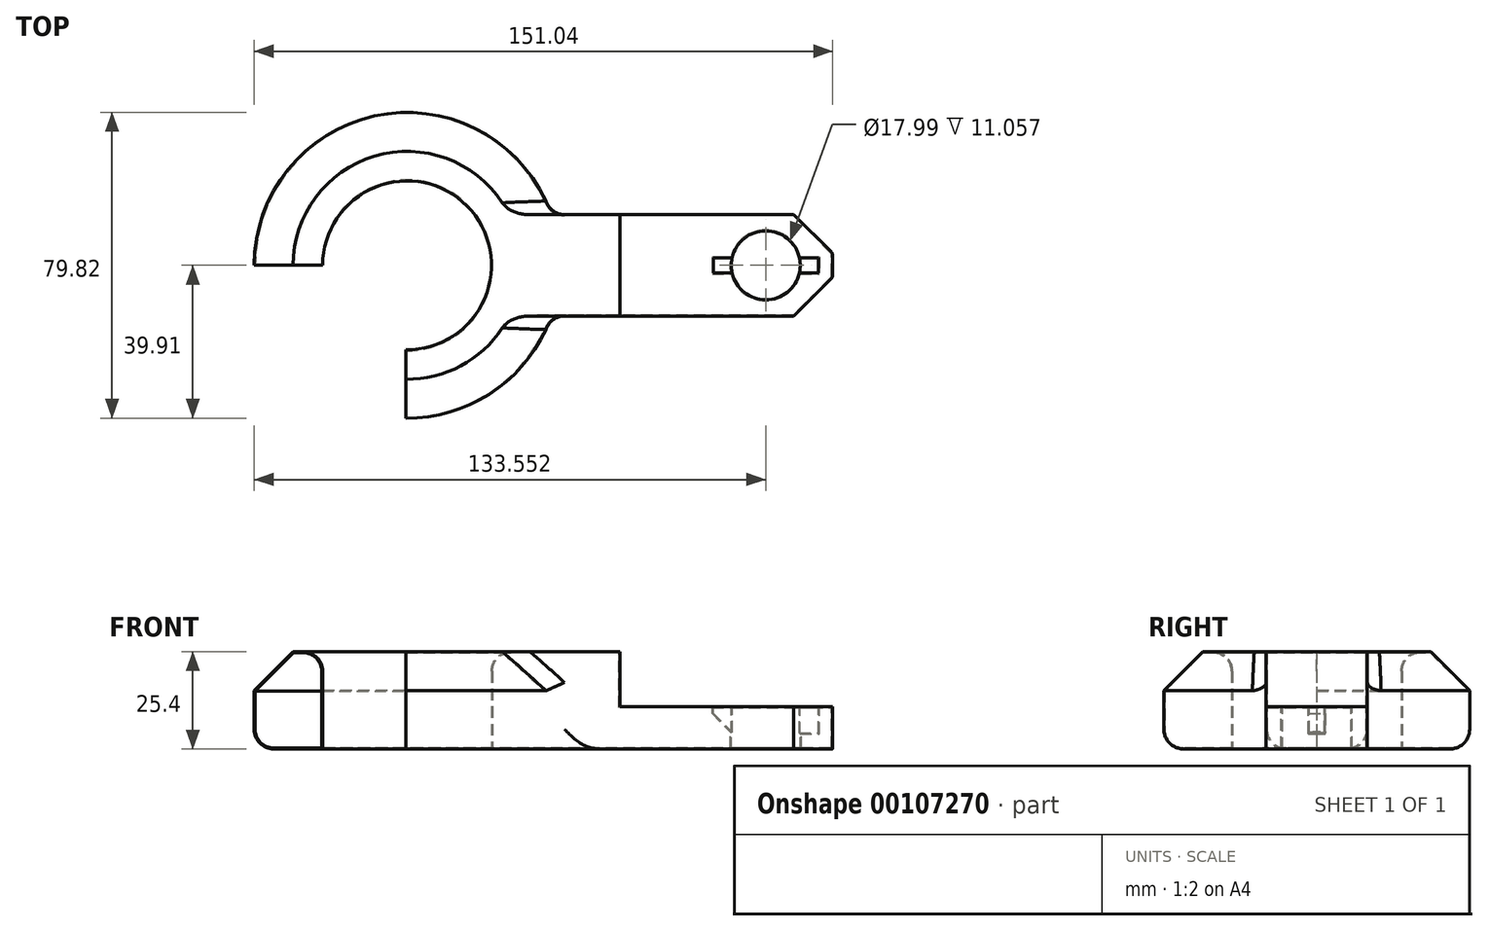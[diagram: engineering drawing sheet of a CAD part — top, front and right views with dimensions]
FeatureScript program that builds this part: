
annotation { "Feature Type Name" : "Feature", "Feature Type Description" : "" }
export const myFeature = defineFeature(function(context is Context, id is Id, definition is map)
    precondition{}
    {
        {
            var Q0;
            Q0=qCreatedBy(makeId("Top.planeOp"),FACE);
            var sketch = newSketch(context, id + "F0", { "sketchPlane" : qUnion([Q0])});
            skLineSegment(sketch, "E0.bottom", {"start": v(55.56, -13.22) * mm, "end": v(-55.56, -13.22) * mm});
            skLineSegment(sketch, "E0.top", {"start": v(55.56, 13.22) * mm, "end": v(-55.56, 13.22) * mm});
            skLineSegment(sketch, "E0.left", {"start": v(55.56, -13.22) * mm, "end": v(55.56, 13.22) * mm});
            skLineSegment(sketch, "E0.right", {"start": v(-55.56, -13.22) * mm, "end": v(-55.56, 13.22) * mm});
            skPoint(sketch, "E0.middle", {"position": v(0, 0) * mm});
            skCircle(sketch, "E1", {"center": v(-55.56, 0) * mm, "radius": 39.91 * mm});
            skCircle(sketch, "E2", {"center": v(-55.56, 0) * mm, "radius": 22.04 * mm});
            skSolve(sketch);
        }
        {
            var Q0;
            {var subQ0=sQuery(id+"F0.wireOp",EDGE,"E1");var subQ1=sQuery(id+"F0.wireOp",EDGE,"E0.bottom");var subQ2=makeQuery(id+"F0.imprint","INTERSECT",VERTEX,{"derivedFrom":[subQ1,subQ0]});Q0=makeQuery(id+"F0.imprint","IMPRINT",FACE,{"disambiguationData":[TD([[makeQuery(id+"F0.imprint","IMPRINT",EDGE,{"disambiguationData":[TD([[subQ2,-1.0]])],"derivedFrom":subQ1}),1.0]])]});}
            var Q1;
            {var subQ0=sQuery(id+"F0.wireOp",EDGE,"E1");var subQ1=sQuery(id+"F0.wireOp",EDGE,"E0.bottom");var subQ2=makeQuery(id+"F0.imprint","INTERSECT",VERTEX,{"derivedFrom":[subQ1,subQ0]});Q1=makeQuery(id+"F0.imprint","IMPRINT",FACE,{"disambiguationData":[TD([[makeQuery(id+"F0.imprint","IMPRINT",EDGE,{"disambiguationData":[TD([[subQ2,-1.0]])],"derivedFrom":subQ1}),-1.0]])]});}
            var Q2;
            {var subQ0=sQuery(id+"F0.wireOp",EDGE,"E0.left");Q2=makeQuery(id+"F0.imprint","IMPRINT",FACE,{"disambiguationData":[TD([[makeQuery(id+"F0.imprint","IMPRINT",EDGE,{"derivedFrom":subQ0}),1.0]])]});}
            extrude(context, id + "F1", {"entities" : qUnion([Q0, Q1, Q2]), "depth" : 25.4 * mm});
        }
        {
            var Q0;
            Q0=makeQuery(id+"F1.opExtrude","CAP_FACE",FACE,{"disambiguationData":[OSD([sQuery(id+"F0.wireOp",EDGE,"E0.bottom"),sQuery(id+"F0.wireOp",EDGE,"E0.top"),sQuery(id+"F0.wireOp",EDGE,"E0.left"),sQuery(id+"F0.wireOp",EDGE,"E1"),sQuery(id+"F0.wireOp",EDGE,"E2")])],"isStart":false});
            var sketch = newSketch(context, id + "F2", { "sketchPlane" : qUnion([Q0])});
            skLineSegment(sketch, "E3.bottom", {"start": v(12.25, 19.58) * mm, "end": v(60.23, 19.58) * mm});
            skLineSegment(sketch, "E3.top", {"start": v(12.25, -22.04) * mm, "end": v(60.23, -22.04) * mm});
            skLineSegment(sketch, "E3.left", {"start": v(12.25, 19.58) * mm, "end": v(12.25, -22.04) * mm});
            skLineSegment(sketch, "E3.right", {"start": v(60.23, 19.58) * mm, "end": v(60.23, -22.04) * mm});
            skSolve(sketch);
        }
        {
            var Q0;
            {var subQ5=makeQuery(id+"F1.opExtrude","CAP_EDGE",EDGE,{"disambiguationData":[OSD([sQuery(id+"F0.wireOp",EDGE,"E0.left")])],"isStart":false});Q0=makeQuery(id+"F2.imprint","IMPRINT",FACE,{"disambiguationData":[TD([[makeQuery(id+"F2.imprint","IMPRINT",EDGE,{"derivedFrom":subQ5}),1.0]])]});}
            extrude(context, id + "F3", {"entities" : qUnion([Q0]), "operationType" : NewBodyOperationType.ADD, "oppositeDirection" : true, "depth" : 15.04 * mm});
        }
        {
            var Q0;
            Q0=makeQuery(id+"F1.opExtrude","CAP_FACE",FACE,{"disambiguationData":[OSD([sQuery(id+"F0.wireOp",EDGE,"E0.bottom"),sQuery(id+"F0.wireOp",EDGE,"E0.top"),sQuery(id+"F0.wireOp",EDGE,"E0.left"),sQuery(id+"F0.wireOp",EDGE,"E1"),sQuery(id+"F0.wireOp",EDGE,"E2")])],"isStart":false});
            var sketch = newSketch(context, id + "F4", { "sketchPlane" : qUnion([Q0])});
            skLineSegment(sketch, "E4.bottom", {"start": v(0, 13.22) * mm, "end": v(55.56, 13.22) * mm});
            skLineSegment(sketch, "E4.top", {"start": v(0, -13.22) * mm, "end": v(55.56, -13.22) * mm});
            skLineSegment(sketch, "E4.left", {"start": v(0, 13.22) * mm, "end": v(0, -13.22) * mm});
            skLineSegment(sketch, "E4.right", {"start": v(55.56, 13.22) * mm, "end": v(55.56, -13.22) * mm});
            skSolve(sketch);
        }
        {
            var Q0;
            Q0=makeQuery(id+"F4.imprint","IMPRINT",FACE,{"disambiguationData":[TD([[makeQuery(id+"F4.imprint","IMPRINT",EDGE,{"derivedFrom":sQuery(id+"F4.wireOp",EDGE,"E4.bottom")}),1.0]])]});
            extrude(context, id + "F5", {"entities" : qUnion([Q0]), "operationType" : NewBodyOperationType.REMOVE, "oppositeDirection" : true, "depth" : 14.34 * mm});
        }
        {
            var Q0;
            Q0=makeQuery(id+"F5.boolean.opBoolean","COPY",EDGE,{"derivedFrom":makeQuery(id+"F5.opExtrude","CAP_EDGE",EDGE,{"disambiguationData":[OSD([sQuery(id+"F4.wireOp",EDGE,"E4.left")])],"isStart":true})});
            var Q1;
            Q1=makeQuery(id+"F1.opExtrude","CAP_EDGE",EDGE,{"disambiguationData":[OSD([sQuery(id+"F0.wireOp",EDGE,"E1")])],"isStart":false});
            var Q2;
            Q2=makeQuery(id+"F1.opExtrude","SWEPT_EDGE",EDGE,{"disambiguationData":[OSD([sQuery(id+"F0.wireOp",EDGE,"E0.bottom"),sQuery(id+"F0.wireOp",EDGE,"E0.left")])]});
            var Q3;
            Q3=makeQuery(id+"F1.opExtrude","SWEPT_EDGE",EDGE,{"disambiguationData":[OSD([sQuery(id+"F0.wireOp",EDGE,"E0.top"),sQuery(id+"F0.wireOp",EDGE,"E0.left")])]});
            chamfer(context, id + "F6", {"entities" : qUnion([Q0, Q1, Q2, Q3]), "width" : 10.16 * mm, "tangentPropagation" : true});
        }
        {
            var Q0;
            Q0=makeQuery(id+"F6.opChamfer","BLEND_EDGE",EDGE,{"blendedFrom":[makeQuery(id+"F1.opExtrude","CAP_EDGE",EDGE,{"disambiguationData":[OSD([sQuery(id+"F0.wireOp",EDGE,"E1")])],"isStart":false}),makeQuery(id+"F1.opExtrude","SWEPT_FACE",FACE,{"disambiguationData":[OSD([sQuery(id+"F0.wireOp",EDGE,"E0.top")])]})],"blendedInto":[makeQuery(id+"F1.opExtrude","SWEPT_FACE",FACE,{"disambiguationData":[OSD([sQuery(id+"F0.wireOp",EDGE,"E0.top")])]})]});
            var Q1;
            Q1=makeQuery(id+"F1.opExtrude","SWEPT_EDGE",EDGE,{"disambiguationData":[OSD([sQuery(id+"F0.wireOp",EDGE,"E0.top"),sQuery(id+"F0.wireOp",EDGE,"E1")])]});
            var Q2;
            Q2=makeQuery(id+"F1.opExtrude","SWEPT_EDGE",EDGE,{"disambiguationData":[OSD([sQuery(id+"F0.wireOp",EDGE,"E0.bottom"),sQuery(id+"F0.wireOp",EDGE,"E1")])]});
            var Q3;
            Q3=makeQuery(id+"F6.opChamfer","BLEND_EDGE",EDGE,{"blendedFrom":[makeQuery(id+"F1.opExtrude","CAP_EDGE",EDGE,{"disambiguationData":[OSD([sQuery(id+"F0.wireOp",EDGE,"E1")])],"isStart":false}),makeQuery(id+"F1.opExtrude","SWEPT_FACE",FACE,{"disambiguationData":[OSD([sQuery(id+"F0.wireOp",EDGE,"E0.bottom")])]})],"blendedInto":[makeQuery(id+"F1.opExtrude","SWEPT_FACE",FACE,{"disambiguationData":[OSD([sQuery(id+"F0.wireOp",EDGE,"E0.bottom")])]})]});
            var Q4;
            Q4=makeQuery(id+"F6.opChamfer","BLEND_EDGE",EDGE,{"blendedFrom":[makeQuery(id+"F5.boolean.opBoolean","COPY",EDGE,{"derivedFrom":makeQuery(id+"F5.opExtrude","CAP_EDGE",EDGE,{"disambiguationData":[OSD([sQuery(id+"F4.wireOp",EDGE,"E4.left")])],"isStart":true})}),makeQuery(id+"F1.opExtrude","CAP_FACE",FACE,{"disambiguationData":[OSD([sQuery(id+"F0.wireOp",EDGE,"E0.bottom"),sQuery(id+"F0.wireOp",EDGE,"E0.top"),sQuery(id+"F0.wireOp",EDGE,"E0.left"),sQuery(id+"F0.wireOp",EDGE,"E1"),sQuery(id+"F0.wireOp",EDGE,"E2")])],"isStart":false})],"blendedInto":[makeQuery(id+"F1.opExtrude","CAP_FACE",FACE,{"disambiguationData":[OSD([sQuery(id+"F0.wireOp",EDGE,"E0.bottom"),sQuery(id+"F0.wireOp",EDGE,"E0.top"),sQuery(id+"F0.wireOp",EDGE,"E0.left"),sQuery(id+"F0.wireOp",EDGE,"E1"),sQuery(id+"F0.wireOp",EDGE,"E2")])],"isStart":false})]});
            var Q5;
            Q5=makeQuery(id+"F1.opExtrude","CAP_EDGE",EDGE,{"disambiguationData":[OSD([sQuery(id+"F0.wireOp",EDGE,"E2")])],"isStart":false});
            var Q6;
            Q6=makeQuery(id+"F1.opExtrude","CAP_EDGE",EDGE,{"disambiguationData":[OSD([sQuery(id+"F0.wireOp",EDGE,"E1")])],"isStart":true});
            fillet(context, id + "F7", {"entities" : qUnion([Q0, Q1, Q2, Q3, Q4, Q5, Q6]), "radius" : 5.08 * mm, "tangentPropagation" : true, "allowEdgeOverflow" : false});
        }
        {
            var Q0;
            Q0=makeQuery(id+"F5.boolean.opBoolean","COPY",FACE,{"derivedFrom":makeQuery(id+"F5.opExtrude","CAP_FACE",FACE,{"disambiguationData":[OSD([sQuery(id+"F4.wireOp",EDGE,"E4.bottom"),sQuery(id+"F4.wireOp",EDGE,"E4.top"),sQuery(id+"F4.wireOp",EDGE,"E4.left"),sQuery(id+"F4.wireOp",EDGE,"E4.right")])],"isStart":false})});
            var sketch = newSketch(context, id + "F8", { "sketchPlane" : qUnion([Q0])});
            skCircle(sketch, "E5", {"center": v(38.07, 0) * mm, "radius": 9 * mm});
            skSolve(sketch);
        }
        {
            var Q0;
            Q0=makeQuery(id+"F8.imprint","IMPRINT",FACE,{"disambiguationData":[TD([[makeQuery(id+"F8.imprint","IMPRINT",EDGE,{"derivedFrom":sQuery(id+"F8.wireOp",EDGE,"E5")}),1.0]])]});
            extrude(context, id + "F9", {"entities" : qUnion([Q0]), "operationType" : NewBodyOperationType.REMOVE, "oppositeDirection" : true, "depth" : 25.4 * mm});
        }
        {
            var Q0;
            Q0=makeQuery(id+"F5.boolean.opBoolean","COPY",FACE,{"derivedFrom":makeQuery(id+"F5.opExtrude","CAP_FACE",FACE,{"disambiguationData":[OSD([sQuery(id+"F4.wireOp",EDGE,"E4.bottom"),sQuery(id+"F4.wireOp",EDGE,"E4.top"),sQuery(id+"F4.wireOp",EDGE,"E4.left"),sQuery(id+"F4.wireOp",EDGE,"E4.right")])],"isStart":false})});
            var sketch = newSketch(context, id + "F10", { "sketchPlane" : qUnion([Q0])});
            skLineSegment(sketch, "E6.bottom", {"start": v(24.33, 2) * mm, "end": v(51.82, 2) * mm});
            skLineSegment(sketch, "E6.top", {"start": v(24.33, -2) * mm, "end": v(51.82, -2) * mm});
            skLineSegment(sketch, "E6.left", {"start": v(24.33, 2) * mm, "end": v(24.33, -2) * mm});
            skLineSegment(sketch, "E6.right", {"start": v(51.82, 2) * mm, "end": v(51.82, -2) * mm});
            skPoint(sketch, "E6.middle", {"position": v(38.07, 0) * mm});
            skSolve(sketch);
        }
        {
            var Q0;
            {var subQ0=sQuery(id+"F10.wireOp",EDGE,"E6.right");Q0=makeQuery(id+"F10.imprint","IMPRINT",FACE,{"disambiguationData":[TD([[makeQuery(id+"F10.imprint","IMPRINT",EDGE,{"derivedFrom":subQ0}),-1.0]])]});}
            var Q1;
            {var subQ0=sQuery(id+"F10.wireOp",EDGE,"E6.left");Q1=makeQuery(id+"F10.imprint","IMPRINT",FACE,{"disambiguationData":[TD([[makeQuery(id+"F10.imprint","IMPRINT",EDGE,{"derivedFrom":subQ0}),1.0]])]});}
            extrude(context, id + "F11", {"entities" : qUnion([Q0, Q1]), "operationType" : NewBodyOperationType.REMOVE, "oppositeDirection" : true, "depth" : 6.82 * mm});
        }
        {
            var Q0;
            Q0=makeQuery(id+"F11.boolean.opBoolean","COPY",EDGE,{"derivedFrom":makeQuery(id+"F11.opExtrude","CAP_EDGE",EDGE,{"disambiguationData":[OSD([sQuery(id+"F10.wireOp",EDGE,"E6.left")])],"isStart":false})});
            var Q1;
            {var subQ0=sQuery(id+"F8.wireOp",EDGE,"E5");var subQ1=makeQuery(id+"F9.boolean.opBoolean","COPY",EDGE,{"derivedFrom":makeQuery(id+"F9.opExtrude","CAP_EDGE",EDGE,{"disambiguationData":[OSD([subQ0])],"isStart":true})});Q1=makeQuery(id+"F11.boolean.opBoolean","COPY",EDGE,{"derivedFrom":makeQuery(id+"F11.opExtrude","CAP_EDGE",EDGE,{"disambiguationData":[OSD([subQ0]),TDD([makeQuery(id+"F10.imprint","IMPRINT",EDGE,{"disambiguationData":[TD([[makeQuery(id+"F10.imprint","INTERSECT",VERTEX,{"disambiguationData":[OD(1.0)],"derivedFrom":[subQ1,sQuery(id+"F10.wireOp",EDGE,"E6.bottom")]}),1.0]])],"derivedFrom":subQ1})])],"isStart":false})});}
            chamfer(context, id + "F12", {"entities" : qUnion([Q0, Q1]), "width" : 5.08 * mm, "tangentPropagation" : true});
        }
        {
            var Q0;
            {var subQ0=sQuery(id+"F8.wireOp",EDGE,"E5");var subQ1=sQuery(id+"F10.wireOp",EDGE,"E6.top");var subQ2=makeQuery(id+"F9.boolean.opBoolean","COPY",EDGE,{"derivedFrom":makeQuery(id+"F9.opExtrude","CAP_EDGE",EDGE,{"disambiguationData":[OSD([subQ0])],"isStart":true})});Q0=makeQuery(id+"F11.boolean.opBoolean","SPLIT",EDGE,{"disambiguationData":[TD([makeQuery(id+"F11.opExtrude","SWEPT_FACE",FACE,{"disambiguationData":[OSD([subQ1]),TDD([makeQuery(id+"F10.imprint","IMPRINT",EDGE,{"disambiguationData":[TD([[makeQuery(id+"F10.imprint","INTERSECT",VERTEX,{"derivedFrom":[subQ1,sQuery(id+"F10.wireOp",EDGE,"E6.left")]}),-1.0]])],"derivedFrom":subQ1})])]})])],"derivedFrom":subQ2});}
            var Q1;
            {var subQ0=sQuery(id+"F8.wireOp",EDGE,"E5");var subQ1=sQuery(id+"F10.wireOp",EDGE,"E6.bottom");var subQ2=makeQuery(id+"F9.boolean.opBoolean","COPY",EDGE,{"derivedFrom":makeQuery(id+"F9.opExtrude","CAP_EDGE",EDGE,{"disambiguationData":[OSD([subQ0])],"isStart":true})});Q1=makeQuery(id+"F11.boolean.opBoolean","SPLIT",EDGE,{"disambiguationData":[TD([makeQuery(id+"F11.opExtrude","SWEPT_FACE",FACE,{"disambiguationData":[OSD([subQ1]),TDD([makeQuery(id+"F10.imprint","IMPRINT",EDGE,{"disambiguationData":[TD([[makeQuery(id+"F10.imprint","INTERSECT",VERTEX,{"derivedFrom":[subQ1,sQuery(id+"F10.wireOp",EDGE,"E6.left")]}),-1.0]])],"derivedFrom":subQ1})])]})])],"derivedFrom":subQ2});}
            var Q2;
            {var subQ0=sQuery(id+"F0.wireOp",EDGE,"E0.left");Q2=makeQuery(id+"F6.opChamfer","BLEND_EDGE",EDGE,{"blendedFrom":[makeQuery(id+"F1.opExtrude","SWEPT_EDGE",EDGE,{"disambiguationData":[OSD([sQuery(id+"F0.wireOp",EDGE,"E0.bottom"),subQ0])]}),makeQuery(id+"F1.opExtrude","SWEPT_FACE",FACE,{"disambiguationData":[OSD([subQ0])]})],"blendedInto":[makeQuery(id+"F1.opExtrude","SWEPT_FACE",FACE,{"disambiguationData":[OSD([subQ0])]})]});}
            var Q3;
            {var subQ0=sQuery(id+"F0.wireOp",EDGE,"E0.left");Q3=makeQuery(id+"F6.opChamfer","BLEND_EDGE",EDGE,{"blendedFrom":[makeQuery(id+"F1.opExtrude","SWEPT_EDGE",EDGE,{"disambiguationData":[OSD([sQuery(id+"F0.wireOp",EDGE,"E0.top"),subQ0])]}),makeQuery(id+"F1.opExtrude","SWEPT_FACE",FACE,{"disambiguationData":[OSD([subQ0])]})],"blendedInto":[makeQuery(id+"F1.opExtrude","SWEPT_FACE",FACE,{"disambiguationData":[OSD([subQ0])]})]});}
            var Q4;
            Q4=makeQuery(id+"F5.boolean.opBoolean","COPY",EDGE,{"derivedFrom":makeQuery(id+"F5.opExtrude","SWEPT_EDGE",EDGE,{"disambiguationData":[OSD([sQuery(id+"F0.wireOp",EDGE,"E0.top"),sQuery(id+"F4.wireOp",EDGE,"E4.bottom"),sQuery(id+"F4.wireOp",EDGE,"E4.left")])]})});
            var Q5;
            Q5=makeQuery(id+"F5.boolean.opBoolean","COPY",EDGE,{"derivedFrom":makeQuery(id+"F5.opExtrude","SWEPT_EDGE",EDGE,{"disambiguationData":[OSD([sQuery(id+"F0.wireOp",EDGE,"E0.bottom"),sQuery(id+"F4.wireOp",EDGE,"E4.top"),sQuery(id+"F4.wireOp",EDGE,"E4.left")])]})});
            fillet(context, id + "F13", {"entities" : qUnion([Q0, Q1, Q2, Q3, Q4, Q5]), "radius" : 1.27 * mm, "tangentPropagation" : true, "allowEdgeOverflow" : false});
        }
        {
            var Q0;
            Q0=qCreatedBy(makeId("Top.planeOp"),FACE);
            var sketch = newSketch(context, id + "F14", { "sketchPlane" : qUnion([Q0])});
            skLineSegment(sketch, "E7.bottom", {"start": v(-55.88, 0) * mm, "end": v(-116.84, 0) * mm});
            skLineSegment(sketch, "E7.top", {"start": v(-55.88, -50.8) * mm, "end": v(-116.84, -50.8) * mm});
            skLineSegment(sketch, "E7.left", {"start": v(-55.88, 0) * mm, "end": v(-55.88, -50.8) * mm});
            skLineSegment(sketch, "E7.right", {"start": v(-116.84, 0) * mm, "end": v(-116.84, -50.8) * mm});
            skSolve(sketch);
        }
        {
            var Q0;
            Q0=makeQuery(id+"F14.imprint","IMPRINT",FACE,{"disambiguationData":[TD([[makeQuery(id+"F14.imprint","IMPRINT",EDGE,{"derivedFrom":sQuery(id+"F14.wireOp",EDGE,"E7.bottom")}),1.0]])]});
            extrude(context, id + "F15", {"entities" : qUnion([Q0]), "operationType" : NewBodyOperationType.REMOVE, "depth" : 25.4 * mm});
        }
        {
            var Q0;
            Q0=makeQuery(id+"F15.boolean.opBoolean","COPY",FACE,{"derivedFrom":makeQuery(id+"F15.opExtrude","SWEPT_FACE",FACE,{"disambiguationData":[OSD([sQuery(id+"F14.wireOp",EDGE,"E7.bottom")])]})});
            var Q1;
            Q1=makeQuery(id+"F15.boolean.opBoolean","COPY",FACE,{"derivedFrom":makeQuery(id+"F15.opExtrude","SWEPT_FACE",FACE,{"disambiguationData":[OSD([sQuery(id+"F14.wireOp",EDGE,"E7.left")])]})});
            shell(context, id + "F16", {"entities" : qUnion([Q0, Q1]), "thickness" : 0.25 * mm});
        }
    });
